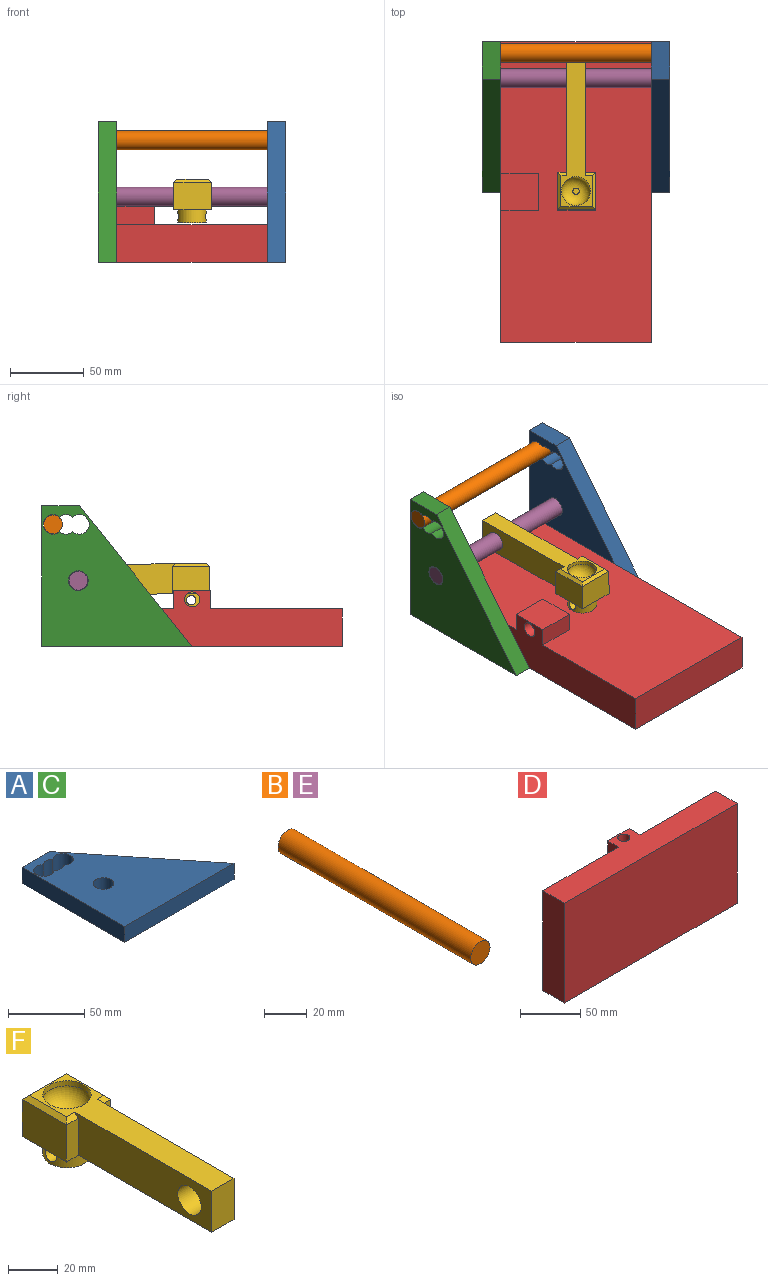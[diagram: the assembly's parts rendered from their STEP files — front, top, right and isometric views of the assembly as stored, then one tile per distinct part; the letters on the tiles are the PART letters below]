
ASSEMBLY  parts=6 mates=5
PART A: 11 faces, bbox 101.6x95.3x12.7 mm
  f0: plane 25.4x12.7mm, normal (0,1,0), area 322.6mm2, adj f1,f8,f9,f10
  f1: plane 95.25x12.7mm, normal (-1,0,0), area 1209.7mm2, adj f0,f2,f9,f10
  f2: plane 101.6x12.7mm, normal (0,-1,0), area 1290.3mm2, adj f1,f8,f9,f10
  f3: cylinder r=6.67mm len=12.7mm, axis (0,0,-1), area 123.6mm2, adj f4,f6,f9,f10
  f4: cylinder r=6.67mm len=13.34mm, axis (0,0,-1), area 389.6mm2, adj f3,f5,f9,f10
  f5: cylinder r=6.67mm len=12.7mm, axis (0,0,-1), area 123.6mm2, adj f4,f6,f9,f10
  f6: cylinder r=6.67mm len=13.34mm, axis (0,0,-1), area 389.6mm2, adj f3,f5,f9,f10
  f7: cylinder r=6.67mm len=13.34mm, axis (0,0,-1), area 532mm2, adj f9,f10
  f8: plane 95.25x76.2mm, normal (0.78,0.62,0), area 1549.1mm2, adj f0,f2,f9,f10
  f9: plane 101.6x95.25mm, normal (0,0,1), area 5550.9mm2, adj f0,f1,f2,f3,f4,f5,f6,f7
  f10: plane 101.6x95.25mm, normal (0,0,-1), area 5550.9mm2, adj f0,f1,f2,f3,f4,f5,f6,f7
PART B: 3 faces, bbox 12.7x127x12.7 mm
  f0: cylinder r=6.35mm len=127mm, axis (0,1,0), area 5067.1mm2, adj f1,f2
  f1: plane 12.7x12.7mm, normal (0,-1,0), area 126.7mm2, adj f0
  f2: plane 12.7x12.7mm, normal (0,1,0), area 126.7mm2, adj f0
PART C: same geometry as A
PART D: 11 faces, bbox 203.2x38.1x101.6 mm
  f0: plane 25.4x12.7mm, normal (1,0,0), area 322.6mm2, adj f1,f3,f4,f10
  f1: plane 25.4x25.4mm, normal (0,1,0), area 645.2mm2, adj f0,f2,f3,f4
  f2: plane 25.4x12.7mm, normal (-1,0,0), area 322.6mm2, adj f1,f3,f4,f10
  f3: plane 25.4x12.7mm, normal (0,0,-1), area 241.5mm2, adj f0,f1,f2,f5,f10
  f4: plane 203.2x38.1mm, normal (0,0,1), area 5402.8mm2, adj f0,f1,f2,f5,f6,f8,f9,f10
  f5: cylinder r=5.08mm len=25.4mm, axis (0,0,1), area 810.7mm2, adj f3,f4
  f6: plane 101.6x25.4mm, normal (-1,0,0), area 2580.6mm2, adj f4,f7,f9,f10
  f7: plane 203.2x25.4mm, normal (0,0,-1), area 5161.3mm2, adj f6,f8,f9,f10
  f8: plane 101.6x25.4mm, normal (1,0,0), area 2580.6mm2, adj f4,f7,f9,f10
  f9: plane 203.2x101.6mm, normal (0,-1,0), area 20645.1mm2, adj f4,f6,f7,f8
  f10: plane 203.2x101.6mm, normal (0,1,0), area 20000mm2, adj f0,f2,f3,f4,f6,f7,f8
PART E: same geometry as B
PART F: 22 faces, bbox 25.4x101.6x29.2 mm
  f0: cylinder r=9.77mm len=19.55mm, axis (0,0,1), area 481.7mm2, adj f11,f20,f21
  f1: plane 25.4x18.29mm, normal (-1,0,0), area 464.5mm2, adj f2,f9,f11,f17
  f2: plane 18.29x6.78mm, normal (0,-1,0), area 123.9mm2, adj f1,f3,f11,f15
  f3: plane 78.23x20.32mm, normal (-1,0,0), area 1410.8mm2, adj f2,f4,f10,f11,f14,f15
  f4: plane 20.32x12.7mm, normal (0,-1,0), area 258.1mm2, adj f3,f5,f10,f11
  f5: plane 78.23x20.32mm, normal (1,0,0), area 1410.8mm2, adj f4,f6,f10,f11,f14,f16
  f6: plane 18.29x5.92mm, normal (0,-1,0), area 108.3mm2, adj f5,f7,f11,f16
  f7: plane 25.4x18.29mm, normal (1,0,0), area 464.5mm2, adj f6,f9,f11,f18
  f8: cylinder r=9.77mm len=19.55mm, axis (0,0,-1), area 156mm2, adj f10,f13
  f9: plane 25.4x18.29mm, normal (0,1,0), area 464.5mm2, adj f1,f7,f11,f19
  f10: plane 99.57x21.34mm, normal (0,0,1), area 1148.7mm2, adj f3,f4,f5,f8,f15,f16,f17,f18
  f11: plane 101.6x25.4mm, normal (0,0,-1), area 1312.8mm2, adj f0,f1,f2,f3,f4,f5,f6,f7
  f12: plane 4.31x4.31mm, normal (0,0,1), area 14.6mm2, adj f13
  f13: torus R=2.15mm, axis (0,0,1), area 526.8mm2, adj f8,f12
  f14: cylinder r=6.67mm len=13.34mm, axis (-1,0,0), area 532mm2, adj f3,f5
  f15: plane 6.78x2.03mm, normal (0,-0.71,0.71), area 16.6mm2, adj f2,f3,f10,f17
  f16: plane 5.92x2.03mm, normal (0,-0.71,0.71), area 14.1mm2, adj f5,f6,f10,f18
  f17: plane 25.4x2.03mm, normal (-0.71,0,0.71), area 67.2mm2, adj f1,f10,f15,f19
  f18: plane 25.4x2.03mm, normal (0.71,0,0.71), area 67.2mm2, adj f7,f10,f16,f19
  f19: plane 25.4x2.03mm, normal (0,0.71,0.71), area 67.2mm2, adj f9,f10,f17,f18
  f20: plane 19.55x19.55mm, normal (0,0,-1), area 300.1mm2, adj f0
  f21: cylinder r=3.17mm len=19.55mm, axis (1,0,0), area 379.4mm2, adj f0
PLACE A rot(axis=(0.58,-0.58,-0.58),120deg) t=(63.5,101.6,0)mm
PLACE B rot(axis=(0,0,-1),90deg) t=(63.5,71.6,44.48)mm
PLACE C rot(axis=(0.58,-0.58,-0.58),120deg) t=(-50.8,101.6,0)mm
PLACE D rot(axis=(0.58,-0.58,-0.58),120deg) t=(44.61,0.21,25.4)mm
PLACE E rot(axis=(-0.58,0.58,0.58),120deg) t=(-63.5,38.76,22.07)mm
PLACE F rot(axis=(0,0,-1),180deg) t=(6.35,76.65,34.93)mm
MATE fastened B.f0 <-> C.f4  axis (-1,0,0) through (-63.5,93.98,82.55)mm
MATE fastened C.f10 <-> D.f4  axis (1,0,0) through (-50.8,101.6,0)mm
MATE fastened E.f0 <-> A.f7  axis (1,0,0) through (63.5,76.84,44.45)mm
MATE fastened A.f9 <-> D.f7  axis (-1,0,0) through (50.8,101.6,0)mm
MATE revolute F.f14 <-> E.f0  axis (1,0,0) through (0,76.84,44.45)mm
